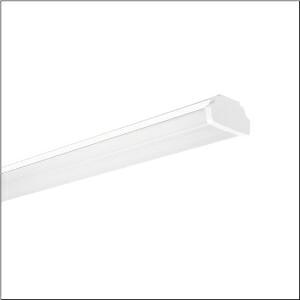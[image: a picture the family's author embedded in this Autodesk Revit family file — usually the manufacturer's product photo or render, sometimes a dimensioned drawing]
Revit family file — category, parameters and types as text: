
# Revit family: modario_r__31_mo_53bm813d2v4085_53ec
name_source: partatom
category: Lighting Fixtures
units: mm (PartAtom-declared; Revit-internal decimal feet)

## family parameters
Cut with Voids When Loaded = No
Host = Face
Light Source = No
Part Type = Normal
Room Calculation Point = No
Round Connector Dimension = Use Diameter
Shared = No

## types (1)
- --- (1 x LED, 8770 lm, 61.8 W, 4000K)
    Apparent Load = 62 VA
    CIE Flux Codes = 61 83 94 92 100
    Color Rendering = 80
    Color Temperature = 4000K
    Default Elevation = 1800 mm
    Description = Modario® 31 MO, luminaire insert, of sheet steel, coil coated, white, length: 1.495mm, width: 81mm, height: 82mm, 5x system unit, system units: 299mm, LED rated luminous flux: 8.770lm, light colour: 840, control gear: DALI 2, control gear: ECG DALI, with plug, 5-pole, with phase selection, mains connection: 220..240V, AC, 50/60Hz, rated input power: 62W, through-wiring accessed according to module size, primary optical cover: cover, of PMMA, light emission: direct distribution, primary light characteristic: symmetric, protection rating (complete): IP20, protection rating (LED compartment): IP50, insulation class (complete): insulation class I (protective earthing), certification: CE, ENEC, VDE, UKCA, impact resistance: IK03, permissible ambient temperature for indoor applications: -25..+30°C, corresponds to IFS (International Featured Standards) requirements for safety and quality in the food industry, reducing of maximum allowable ambient temperature of 5°C with ceiling mounting, packaging unit: 1 piece
    Height = 92 mm
    Lamp = 1 x LED
    Lamp Light Flux = 8770 lm
    Lamp Power = 61.8 W
    Lamp count = 1
    Length = 1495 mm
    Luminous efficacy = 142 lm/W
    Manufacturer = Siteco
    ModVariant = No
    Model = 53BM813D2V4085
    Mounting Place = Ceiling
    Mounting Type = Pendant
    Number of Poles = 1
    OnlyDefault = Yes
    Power Factor = 1
    Product Name = Modario® 31 MO
    Product group = luminaire insert
    ProductGroupID = 901
    Protection Class = Protection class I
    Protection Degree = IP 20
    RLX_Detail_Level = 1
    RLX_Emergency_Light_Flux = 0 lm
    RLX_Emergency_Type = 0
    RLX_Emergency_Type_DB = No
    RlxData = <blob elided: 42405 chars, md5=06a5dce4>
    Socket = socket
    Standby Power = 0 W
    System Light Flux = 8770 lm
    System Power = 62 W
    Type Comments = factory setting: luminous flux: 100 % | dim-lin: 254 | 500 mA
    Type Image = l_1300283.jpg
    URL = http://relux.com
    VarID = @adj_148825
    Voltage = 0 V
    Weight = 0.00 kg
    Width = 81 mm

## geometry (parser evidence)
native form markers: Blend x4, Sweep x12
no freeform markers — native parametric forms only
